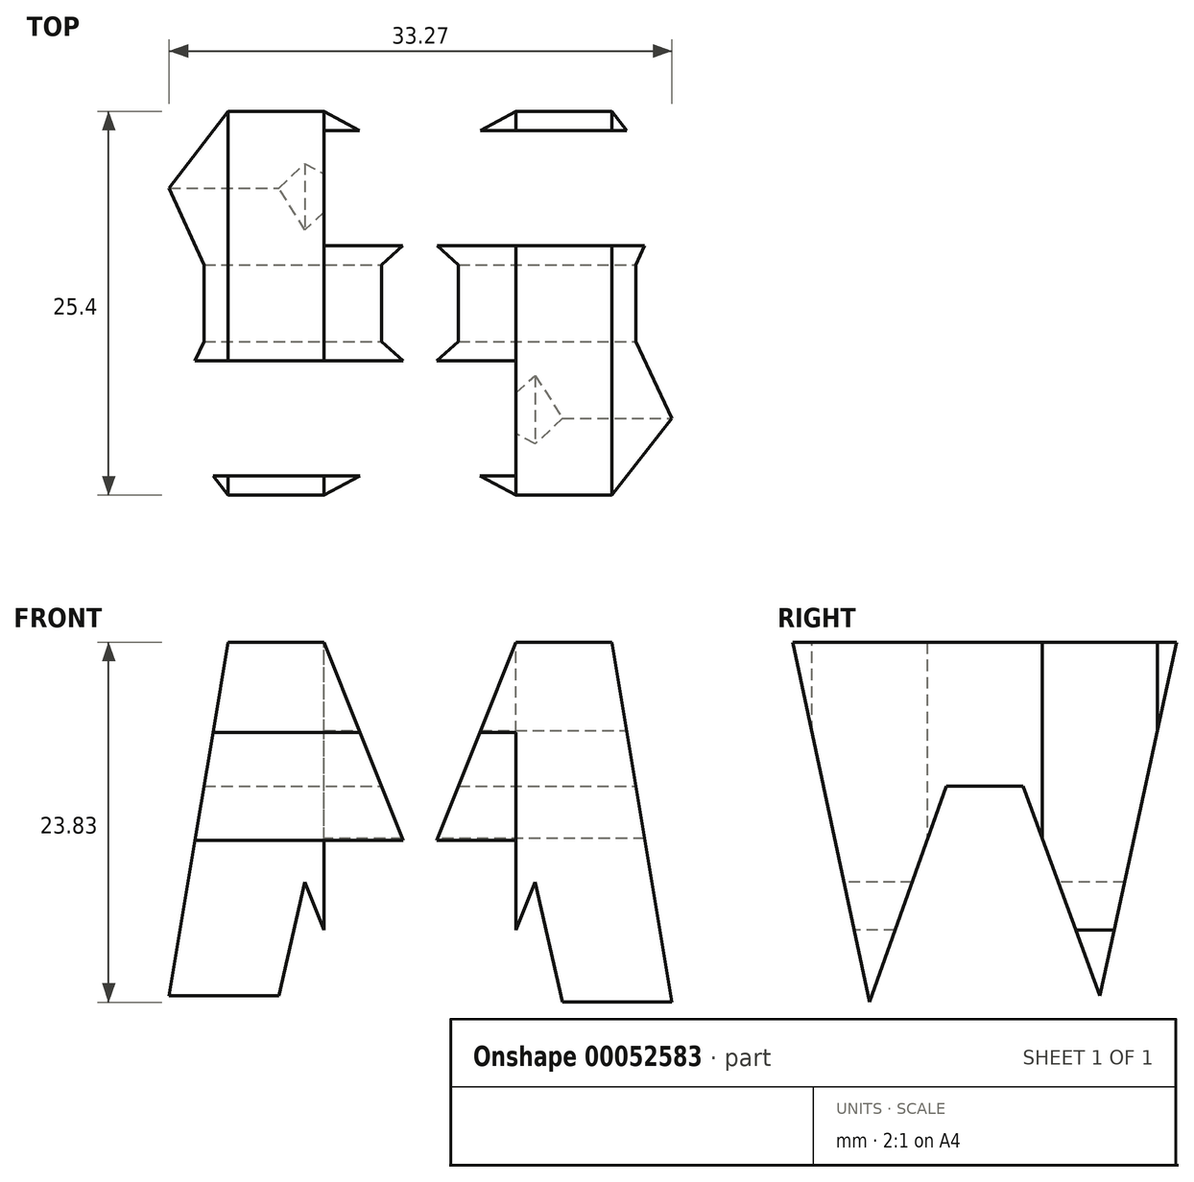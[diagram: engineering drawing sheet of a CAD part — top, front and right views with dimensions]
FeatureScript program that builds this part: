
annotation { "Feature Type Name" : "Feature", "Feature Type Description" : "" }
export const myFeature = defineFeature(function(context is Context, id is Id, definition is map)
    precondition{}
    {
        {
            var Q0;
            Q0=qCreatedBy(makeId("Front.planeOp"),FACE);
            var sketch = newSketch(context, id + "F0", { "sketchPlane" : qUnion([Q0])});
            skLineSegment(sketch, "E0", {"start": v(0, 0) * mm, "end": v(0, 38.1) * mm});
            skLineSegment(sketch, "E1", {"start": v(0, 38.1) * mm, "end": v(38.1, 38.1) * mm});
            skLineSegment(sketch, "E2", {"start": v(38.1, 38.1) * mm, "end": v(38.1, 0) * mm});
            skLineSegment(sketch, "E3", {"start": v(38.1, 0) * mm, "end": v(0, 0) * mm});
            skSolve(sketch);
        }
        {
            var Q0;
            Q0 = qSketchRegion(id + "F0", true);
            extrude(context, id + "F1", {"entities" : qUnion([Q0]), "depth" : 38.1 * mm});
        }
        {
            var Q0;
            Q0=qCreatedBy(makeId("Front.planeOp"),FACE);
            cPlane(context, id + "F2", {"entities" : qUnion([Q0]), "cplaneType" : CPlaneType.OFFSET, "offset" : 38.1 * mm, "width" : 152.4 * mm, "height" : 152.4 * mm});
        }
        {
            var Q0;
            Q0=qCreatedBy(makeId("Top.planeOp"),FACE);
            cPlane(context, id + "F3", {"entities" : qUnion([Q0]), "cplaneType" : CPlaneType.OFFSET, "offset" : 38.1 * mm, "width" : 152.4 * mm, "height" : 152.4 * mm});
        }
        {
            var Q0;
            Q0=qCreatedBy(makeId("Right.planeOp"),FACE);
            cPlane(context, id + "F4", {"entities" : qUnion([Q0]), "cplaneType" : CPlaneType.OFFSET, "offset" : 38.1 * mm, "width" : 152.4 * mm, "height" : 152.4 * mm});
        }
        {
            var Q0;
            Q0=qCreatedBy(id+"F4.planeOp",FACE);
            var sketch = newSketch(context, id + "F5", { "sketchPlane" : qUnion([Q0])});
            skLineSegment(sketch, "E4", {"start": v(0, 0) * mm, "end": v(0, 38.1) * mm});
            skLineSegment(sketch, "E5", {"start": v(0, 38.1) * mm, "end": v(-38.1, 38.1) * mm});
            skLineSegment(sketch, "E6", {"start": v(-38.1, 38.1) * mm, "end": v(-38.1, 0) * mm});
            skLineSegment(sketch, "E7", {"start": v(-38.1, 0) * mm, "end": v(0, 0) * mm});
            skLineSegment(sketch, "E8", {"start": v(-38.1, 38.1) * mm, "end": v(-31.75, 0) * mm});
            skLineSegment(sketch, "E9", {"start": v(-31.75, 38.1) * mm, "end": v(-26.67, 14.27) * mm});
            skLineSegment(sketch, "E10", {"start": v(-26.67, 14.27) * mm, "end": v(-21.59, 28.58) * mm});
            skLineSegment(sketch, "E11", {"start": v(-21.59, 28.58) * mm, "end": v(-16.5, 28.58) * mm});
            skLineSegment(sketch, "E12", {"start": v(-16.5, 28.58) * mm, "end": v(-11.43, 14.7) * mm});
            skLineSegment(sketch, "E13", {"start": v(-11.43, 14.7) * mm, "end": v(-6.35, 38.1) * mm});
            skLineSegment(sketch, "E14", {"start": v(0, 38.1) * mm, "end": v(-6.35, 0) * mm});
            skLineSegment(sketch, "E15", {"start": v(-25.4, 0) * mm, "end": v(-19.05, 15.88) * mm});
            skLineSegment(sketch, "E16", {"start": v(-19.05, 15.88) * mm, "end": v(-12.7, 0) * mm});
            skLineSegment(sketch, "E17", {"start": v(-38.1, 38.1) * mm, "end": v(-31.75, 38.1) * mm});
            skLineSegment(sketch, "E18", {"start": v(-6.35, 38.1) * mm, "end": v(0, 38.1) * mm});
            skLineSegment(sketch, "E19", {"start": v(-6.35, 0) * mm, "end": v(-12.7, 0) * mm});
            skLineSegment(sketch, "E20", {"start": v(-25.4, 0) * mm, "end": v(-31.75, 0) * mm});
            skSolve(sketch);
        }
        {
            var Q0;
            {var subQ0=sQuery(id+"F5.wireOp",EDGE,"E6");Q0=makeQuery(id+"F5.imprint","IMPRINT",FACE,{"disambiguationData":[TD([[makeQuery(id+"F5.imprint","IMPRINT",EDGE,{"derivedFrom":subQ0}),1.0]])]});}
            var Q1;
            Q1=makeQuery(id+"F5.imprint","IMPRINT",FACE,{"disambiguationData":[TD([[makeQuery(id+"F5.imprint","IMPRINT",EDGE,{"derivedFrom":sQuery(id+"F5.wireOp",EDGE,"E5")}),1.0]])]});
            var Q2;
            {var subQ0=sQuery(id+"F5.wireOp",EDGE,"E4");Q2=makeQuery(id+"F5.imprint","IMPRINT",FACE,{"disambiguationData":[TD([[makeQuery(id+"F5.imprint","IMPRINT",EDGE,{"derivedFrom":subQ0}),1.0]])]});}
            var Q3;
            {var subQ0=sQuery(id+"F5.wireOp",EDGE,"E15");Q3=makeQuery(id+"F5.imprint","IMPRINT",FACE,{"disambiguationData":[TD([[makeQuery(id+"F5.imprint","IMPRINT",EDGE,{"derivedFrom":subQ0}),-1.0]])]});}
            extrude(context, id + "F6", {"entities" : qUnion([Q0, Q1, Q2, Q3]), "operationType" : NewBodyOperationType.REMOVE, "oppositeDirection" : true, "depth" : 38.1 * mm});
        }
        {
            var Q0;
            Q0=qCreatedBy(id+"F2.planeOp",FACE);
            var sketch = newSketch(context, id + "F7", { "sketchPlane" : qUnion([Q0])});
            skLineSegment(sketch, "E21", {"start": v(0, 0) * mm, "end": v(38.1, 0) * mm});
            skLineSegment(sketch, "E22", {"start": v(38.1, 0) * mm, "end": v(38.1, 38.1) * mm});
            skLineSegment(sketch, "E23", {"start": v(38.1, 38.1) * mm, "end": v(0, 38.1) * mm});
            skLineSegment(sketch, "E24", {"start": v(0, 38.1) * mm, "end": v(0, 0) * mm});
            skLineSegment(sketch, "E25", {"start": v(0, 0) * mm, "end": v(6.35, 38.1) * mm});
            skLineSegment(sketch, "E26", {"start": v(6.35, 38.1) * mm, "end": v(12.7, 38.1) * mm});
            skLineSegment(sketch, "E27", {"start": v(12.7, 38.1) * mm, "end": v(19.05, 22.22) * mm});
            skLineSegment(sketch, "E28", {"start": v(19.05, 22.22) * mm, "end": v(25.4, 38.1) * mm});
            skLineSegment(sketch, "E29", {"start": v(25.4, 38.1) * mm, "end": v(31.75, 38.1) * mm});
            skLineSegment(sketch, "E30", {"start": v(31.75, 38.1) * mm, "end": v(38.1, 0) * mm});
            skLineSegment(sketch, "E31", {"start": v(31.75, 0) * mm, "end": v(26.67, 22.23) * mm});
            skLineSegment(sketch, "E32", {"start": v(26.67, 22.23) * mm, "end": v(21.59, 9.52) * mm});
            skLineSegment(sketch, "E33", {"start": v(21.59, 9.53) * mm, "end": v(16.51, 9.53) * mm});
            skLineSegment(sketch, "E34", {"start": v(16.51, 9.52) * mm, "end": v(11.43, 22.23) * mm});
            skLineSegment(sketch, "E35", {"start": v(11.43, 22.23) * mm, "end": v(6.35, 0) * mm});
            skSolve(sketch);
        }
        {
            var Q0;
            {var subQ0=sQuery(id+"F7.wireOp",EDGE,"E24");Q0=makeQuery(id+"F7.imprint","IMPRINT",FACE,{"disambiguationData":[TD([[makeQuery(id+"F7.imprint","IMPRINT",EDGE,{"derivedFrom":subQ0}),1.0]])]});}
            var Q1;
            {var subQ0=sQuery(id+"F7.wireOp",EDGE,"E27");Q1=makeQuery(id+"F7.imprint","IMPRINT",FACE,{"disambiguationData":[TD([[makeQuery(id+"F7.imprint","IMPRINT",EDGE,{"derivedFrom":subQ0}),1.0]])]});}
            var Q2;
            {var subQ0=sQuery(id+"F7.wireOp",EDGE,"E22");Q2=makeQuery(id+"F7.imprint","IMPRINT",FACE,{"disambiguationData":[TD([[makeQuery(id+"F7.imprint","IMPRINT",EDGE,{"derivedFrom":subQ0}),1.0]])]});}
            var Q3;
            {var subQ0=sQuery(id+"F7.wireOp",EDGE,"E31");Q3=makeQuery(id+"F7.imprint","IMPRINT",FACE,{"disambiguationData":[TD([[makeQuery(id+"F7.imprint","IMPRINT",EDGE,{"derivedFrom":subQ0}),1.0]])]});}
            extrude(context, id + "F8", {"entities" : qUnion([Q0, Q1, Q2, Q3]), "operationType" : NewBodyOperationType.REMOVE, "oppositeDirection" : true, "depth" : 38.1 * mm});
        }
        {
            var Q0;
            Q0=qCreatedBy(id+"F3.planeOp",FACE);
            var sketch = newSketch(context, id + "F9", { "sketchPlane" : qUnion([Q0])});
            skLineSegment(sketch, "E36", {"start": v(0, 0) * mm, "end": v(38.1, 0) * mm});
            skLineSegment(sketch, "E37", {"start": v(38.1, 0) * mm, "end": v(38.1, -38.1) * mm});
            skLineSegment(sketch, "E38", {"start": v(38.1, -38.1) * mm, "end": v(0, -38.1) * mm});
            skLineSegment(sketch, "E39", {"start": v(0, -38.1) * mm, "end": v(0, 0) * mm});
            skLineSegment(sketch, "E40", {"start": v(38.1, -7.62) * mm, "end": v(12.7, -7.62) * mm});
            skLineSegment(sketch, "E41", {"start": v(12.7, -7.62) * mm, "end": v(12.7, -15.24) * mm});
            skLineSegment(sketch, "E42", {"start": v(12.7, -15.24) * mm, "end": v(38.1, -15.24) * mm});
            skLineSegment(sketch, "E43", {"start": v(38.1, -15.24) * mm, "end": v(38.1, -7.62) * mm});
            skLineSegment(sketch, "E44", {"start": v(0, -22.86) * mm, "end": v(25.4, -22.86) * mm});
            skLineSegment(sketch, "E45", {"start": v(25.4, -22.86) * mm, "end": v(25.4, -30.48) * mm});
            skLineSegment(sketch, "E46", {"start": v(25.4, -30.48) * mm, "end": v(0, -30.48) * mm});
            skLineSegment(sketch, "E47", {"start": v(0, -30.48) * mm, "end": v(0, -22.86) * mm});
            skSolve(sketch);
        }
        {
            var Q0;
            Q0=makeQuery(id+"F9.imprint","IMPRINT",FACE,{"disambiguationData":[TD([[makeQuery(id+"F9.imprint","IMPRINT",EDGE,{"derivedFrom":sQuery(id+"F9.wireOp",EDGE,"E40")}),1.0]])]});
            var Q1;
            Q1=makeQuery(id+"F9.imprint","IMPRINT",FACE,{"disambiguationData":[TD([[makeQuery(id+"F9.imprint","IMPRINT",EDGE,{"derivedFrom":sQuery(id+"F9.wireOp",EDGE,"E44")}),-1.0]])]});
            extrude(context, id + "F10", {"entities" : qUnion([Q0, Q1]), "operationType" : NewBodyOperationType.REMOVE, "oppositeDirection" : true, "depth" : 38.1 * mm});
        }
    });
